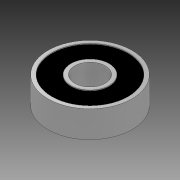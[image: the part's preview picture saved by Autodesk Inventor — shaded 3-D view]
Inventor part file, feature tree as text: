
AUTODESK INVENTOR PART (.ipt)
format: ipt  version: 2020 (Build 240168000, 168)  size: 128,512 bytes
history: native  units: mm
features: revolve x1, sketch x1
ambient origin geometry x8: Origin, YZ Plane, XZ Plane, XY Plane, X Axis, Y Axis, Z Axis, Center Point
bodies: Solid1 (feature_tree)
feature tree (2):
  revolve  "Revolution1"  [1 undecoded]
  sketch  "Sketch1"  dims[d0=4.0mm d2=7.0mm d5=11.0mm d6=0.2mm d7=1.0mm d8=90.0deg]
note: 1 required parameter value undecoded (feature->parameter linkage not recoverable at this tier; creation-order binding heuristic only, values carry confidence <= 0.55)
